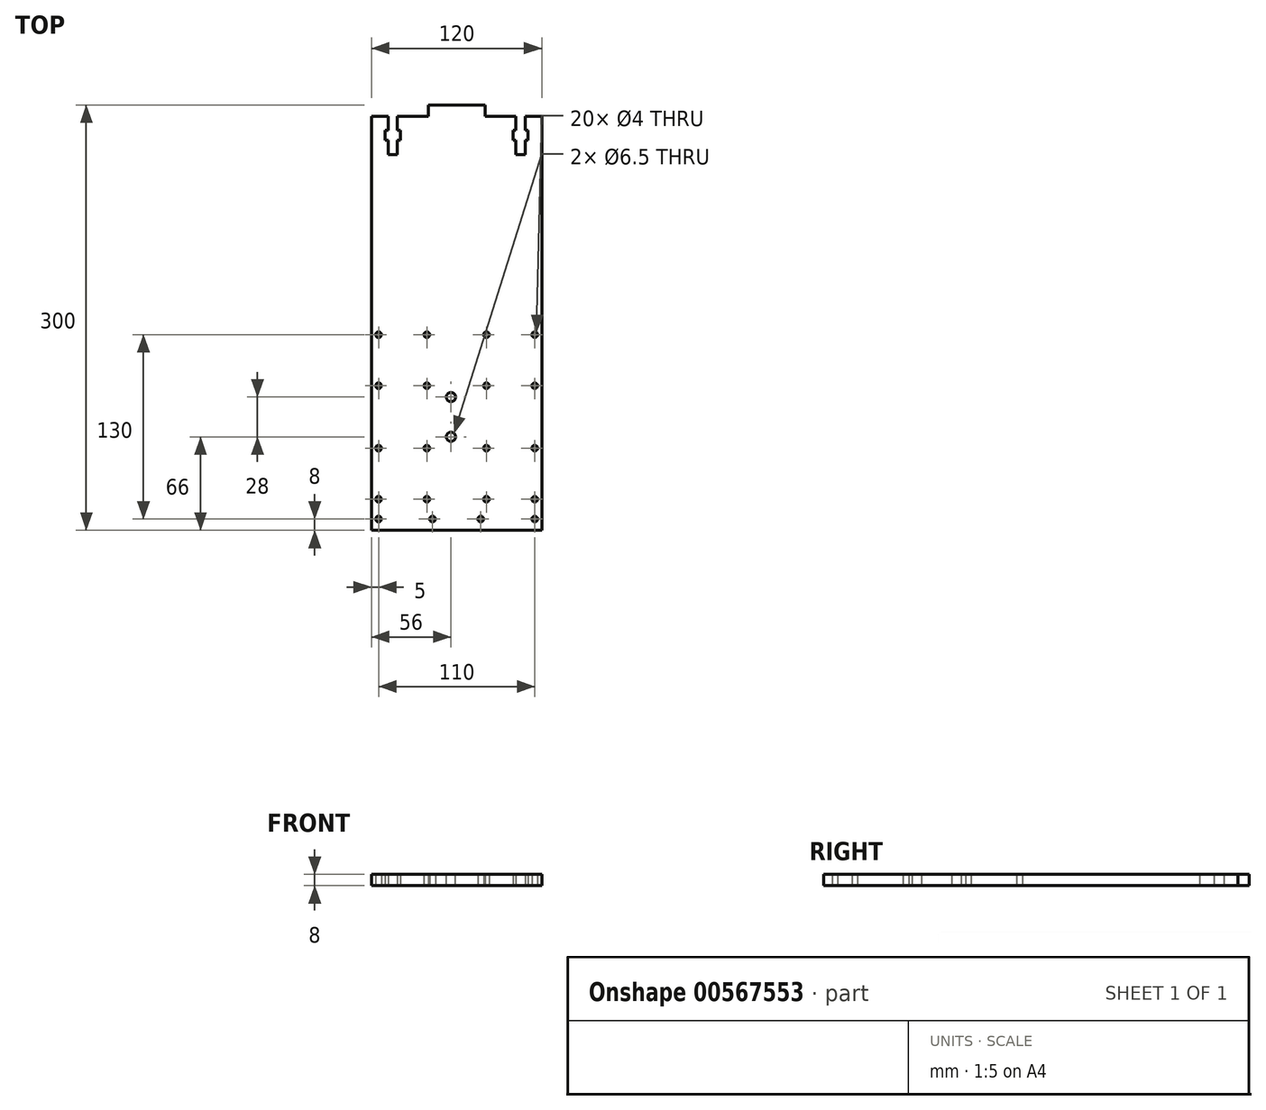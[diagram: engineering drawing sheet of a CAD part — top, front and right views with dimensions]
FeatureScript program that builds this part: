
annotation { "Feature Type Name" : "Feature", "Feature Type Description" : "" }
export const myFeature = defineFeature(function(context is Context, id is Id, definition is map)
    precondition{}
    {
        {
            var Q0;
            Q0=qCreatedBy(makeId("Top.planeOp"),FACE);
            var sketch = newSketch(context, id + "F0", { "sketchPlane" : qUnion([Q0])});
            skLineSegment(sketch, "E0.bottom", {"start": v(60, 212) * mm, "end": v(48.25, 212) * mm});
            skLineSegment(sketch, "E0.top", {"start": v(60, -80) * mm, "end": v(-60, -80) * mm});
            skLineSegment(sketch, "E0.left", {"start": v(60, 212) * mm, "end": v(60, -80) * mm});
            skLineSegment(sketch, "E0.right", {"start": v(-60, 212) * mm, "end": v(-60, -80) * mm});
            skPoint(sketch, "E0.middle", {"position": v(0, 66) * mm});
            skLineSegment(sketch, "E1.bottom", {"start": v(-55, 58) * mm, "end": v(-21, 58) * mm, "construction": true});
            skLineSegment(sketch, "E1.top", {"start": v(-55, 22) * mm, "end": v(-21, 22) * mm, "construction": true});
            skLineSegment(sketch, "E1.left", {"start": v(-55, 58) * mm, "end": v(-55, 22) * mm, "construction": true});
            skLineSegment(sketch, "E1.right", {"start": v(-21, 58) * mm, "end": v(-21, 22) * mm, "construction": true});
            skCircle(sketch, "E2", {"center": v(-55, 58) * mm, "radius": 2 * mm});
            skCircle(sketch, "E3", {"center": v(-21, 58) * mm, "radius": 2 * mm});
            skCircle(sketch, "E4", {"center": v(-21, 22) * mm, "radius": 2 * mm});
            skCircle(sketch, "E5", {"center": v(-55, 22) * mm, "radius": 2 * mm});
            skCircle(sketch, "E6.MirrorC", {"center": v(21, 58) * mm, "radius": 2 * mm});
            skCircle(sketch, "E7.MirrorC", {"center": v(55, 58) * mm, "radius": 2 * mm});
            skCircle(sketch, "E8.MirrorC", {"center": v(55, 22) * mm, "radius": 2 * mm});
            skCircle(sketch, "E9.MirrorC", {"center": v(21, 22) * mm, "radius": 2 * mm});
            skCircle(sketch, "E10.MirrorC", {"center": v(-55, -22) * mm, "radius": 2 * mm});
            skCircle(sketch, "E11.MirrorC", {"center": v(21, -22) * mm, "radius": 2 * mm});
            skCircle(sketch, "E12.MirrorC", {"center": v(55, -22) * mm, "radius": 2 * mm});
            skCircle(sketch, "E13.MirrorC", {"center": v(-21, -22) * mm, "radius": 2 * mm});
            skCircle(sketch, "E14.MirrorC", {"center": v(21, -58) * mm, "radius": 2 * mm});
            skCircle(sketch, "E15.MirrorC", {"center": v(55, -58) * mm, "radius": 2 * mm});
            skCircle(sketch, "E16.MirrorC", {"center": v(-21, -58) * mm, "radius": 2 * mm});
            skCircle(sketch, "E17.MirrorC", {"center": v(-55, -58) * mm, "radius": 2 * mm});
            skCircle(sketch, "E18", {"center": v(-55, -72) * mm, "radius": 2 * mm});
            skCircle(sketch, "E19", {"center": v(-17, -72) * mm, "radius": 2 * mm});
            skCircle(sketch, "E20", {"center": v(17, -72) * mm, "radius": 2 * mm});
            skCircle(sketch, "E21", {"center": v(55, -72) * mm, "radius": 2 * mm});
            skLineSegment(sketch, "E22", {"start": v(20, 220) * mm, "end": v(20, 212) * mm});
            skLineSegment(sketch, "E23", {"start": v(20, 220) * mm, "end": v(-20, 220) * mm});
            skLineSegment(sketch, "E24", {"start": v(-20, 212) * mm, "end": v(-20, 220) * mm});
            skLineSegment(sketch, "E25.trimOffspring", {"start": v(-20, 212) * mm, "end": v(-41.75, 212) * mm});
            skLineSegment(sketch, "E26", {"start": v(-41.75, 212) * mm, "end": v(-41.75, 202) * mm});
            skLineSegment(sketch, "E27", {"start": v(-41.75, 202) * mm, "end": v(-39.75, 202) * mm});
            skLineSegment(sketch, "E28", {"start": v(-39.75, 202) * mm, "end": v(-39.75, 195) * mm});
            skLineSegment(sketch, "E29", {"start": v(-39.75, 195) * mm, "end": v(-41.75, 195) * mm});
            skLineSegment(sketch, "E30", {"start": v(-41.75, 195) * mm, "end": v(-41.75, 185) * mm});
            skLineSegment(sketch, "E31", {"start": v(-41.75, 185) * mm, "end": v(-48.25, 185) * mm});
            skLineSegment(sketch, "E32", {"start": v(-48.25, 185) * mm, "end": v(-48.25, 195) * mm});
            skLineSegment(sketch, "E33", {"start": v(-48.25, 195) * mm, "end": v(-50.25, 195) * mm});
            skLineSegment(sketch, "E34", {"start": v(-50.25, 195) * mm, "end": v(-50.25, 202) * mm});
            skLineSegment(sketch, "E35", {"start": v(-50.25, 202) * mm, "end": v(-48.25, 202) * mm});
            skLineSegment(sketch, "E36", {"start": v(-48.25, 202) * mm, "end": v(-48.25, 212) * mm});
            skLineSegment(sketch, "E37.trimOffspring", {"start": v(-48.25, 212) * mm, "end": v(-60, 212) * mm});
            skLineSegment(sketch, "E38.MirrorCS", {"start": v(41.75, 185) * mm, "end": v(48.25, 185) * mm});
            skLineSegment(sketch, "E39.MirrorCS", {"start": v(41.75, 195) * mm, "end": v(41.75, 185) * mm});
            skLineSegment(sketch, "E40.MirrorCS", {"start": v(48.25, 185) * mm, "end": v(48.25, 195) * mm});
            skLineSegment(sketch, "E41.MirrorCS", {"start": v(48.25, 195) * mm, "end": v(50.25, 195) * mm});
            skLineSegment(sketch, "E42.MirrorCS", {"start": v(39.75, 195) * mm, "end": v(41.75, 195) * mm});
            skLineSegment(sketch, "E43.MirrorCS", {"start": v(39.75, 202) * mm, "end": v(39.75, 195) * mm});
            skLineSegment(sketch, "E44.MirrorCS", {"start": v(50.25, 195) * mm, "end": v(50.25, 202) * mm});
            skLineSegment(sketch, "E45.MirrorCS", {"start": v(50.25, 202) * mm, "end": v(48.25, 202) * mm});
            skLineSegment(sketch, "E46.MirrorCS", {"start": v(41.75, 202) * mm, "end": v(39.75, 202) * mm});
            skLineSegment(sketch, "E47.MirrorCS", {"start": v(41.75, 212) * mm, "end": v(41.75, 202) * mm});
            skLineSegment(sketch, "E48.MirrorCS", {"start": v(48.25, 202) * mm, "end": v(48.25, 212) * mm});
            skLineSegment(sketch, "E49.trimOffspring", {"start": v(41.75, 212) * mm, "end": v(20, 212) * mm});
            skSolve(sketch);
        }
        {
            var Q0;
            Q0 = qSketchRegion(id + "F0", true);
            extrude(context, id + "F1", {"entities" : qUnion([Q0]), "depth" : 8 * mm, "offsetDistance" : 25 * mm});
        }
        {
            var Q0;
            Q0=makeQuery(id+"F1.opExtrude","CAP_FACE",FACE,{"disambiguationData":[OSD([sQuery(id+"F0.wireOp",EDGE,"E0.bottom"),sQuery(id+"F0.wireOp",EDGE,"E0.top"),sQuery(id+"F0.wireOp",EDGE,"E0.left"),sQuery(id+"F0.wireOp",EDGE,"E0.right"),sQuery(id+"F0.wireOp",EDGE,"E2"),sQuery(id+"F0.wireOp",EDGE,"E3"),sQuery(id+"F0.wireOp",EDGE,"E4"),sQuery(id+"F0.wireOp",EDGE,"E5"),sQuery(id+"F0.wireOp",EDGE,"E6.MirrorC"),sQuery(id+"F0.wireOp",EDGE,"E7.MirrorC"),sQuery(id+"F0.wireOp",EDGE,"E8.MirrorC"),sQuery(id+"F0.wireOp",EDGE,"E9.MirrorC"),sQuery(id+"F0.wireOp",EDGE,"E10.MirrorC"),sQuery(id+"F0.wireOp",EDGE,"E11.MirrorC"),sQuery(id+"F0.wireOp",EDGE,"E12.MirrorC"),sQuery(id+"F0.wireOp",EDGE,"E13.MirrorC"),sQuery(id+"F0.wireOp",EDGE,"E14.MirrorC"),sQuery(id+"F0.wireOp",EDGE,"E15.MirrorC"),sQuery(id+"F0.wireOp",EDGE,"E16.MirrorC"),sQuery(id+"F0.wireOp",EDGE,"E17.MirrorC"),sQuery(id+"F0.wireOp",EDGE,"E18"),sQuery(id+"F0.wireOp",EDGE,"E19"),sQuery(id+"F0.wireOp",EDGE,"E20"),sQuery(id+"F0.wireOp",EDGE,"E21"),sQuery(id+"F0.wireOp",EDGE,"E22"),sQuery(id+"F0.wireOp",EDGE,"E23"),sQuery(id+"F0.wireOp",EDGE,"E24"),sQuery(id+"F0.wireOp",EDGE,"E25.trimOffspring"),sQuery(id+"F0.wireOp",EDGE,"E26"),sQuery(id+"F0.wireOp",EDGE,"E27"),sQuery(id+"F0.wireOp",EDGE,"E28"),sQuery(id+"F0.wireOp",EDGE,"E29"),sQuery(id+"F0.wireOp",EDGE,"E30"),sQuery(id+"F0.wireOp",EDGE,"E31"),sQuery(id+"F0.wireOp",EDGE,"E32"),sQuery(id+"F0.wireOp",EDGE,"E33"),sQuery(id+"F0.wireOp",EDGE,"E34"),sQuery(id+"F0.wireOp",EDGE,"E35"),sQuery(id+"F0.wireOp",EDGE,"E36"),sQuery(id+"F0.wireOp",EDGE,"E37.trimOffspring"),sQuery(id+"F0.wireOp",EDGE,"E38.MirrorCS"),sQuery(id+"F0.wireOp",EDGE,"E39.MirrorCS"),sQuery(id+"F0.wireOp",EDGE,"E40.MirrorCS"),sQuery(id+"F0.wireOp",EDGE,"E41.MirrorCS"),sQuery(id+"F0.wireOp",EDGE,"E42.MirrorCS"),sQuery(id+"F0.wireOp",EDGE,"E43.MirrorCS"),sQuery(id+"F0.wireOp",EDGE,"E44.MirrorCS"),sQuery(id+"F0.wireOp",EDGE,"E45.MirrorCS"),sQuery(id+"F0.wireOp",EDGE,"E46.MirrorCS"),sQuery(id+"F0.wireOp",EDGE,"E47.MirrorCS"),sQuery(id+"F0.wireOp",EDGE,"E48.MirrorCS"),sQuery(id+"F0.wireOp",EDGE,"E49.trimOffspring")])],"isStart":false});
            var sketch = newSketch(context, id + "F2", { "sketchPlane" : qUnion([Q0])});
            skCircle(sketch, "E50", {"center": v(-4, 14) * mm, "radius": 3.25 * mm});
            skCircle(sketch, "E51", {"center": v(-4, -14) * mm, "radius": 3.25 * mm});
            skSolve(sketch);
        }
        {
            var Q0;
            Q0 = qSketchRegion(id + "F2", true);
            extrude(context, id + "F3", {"entities" : qUnion([Q0]), "operationType" : NewBodyOperationType.REMOVE, "endBound" : BoundingType.THROUGH_ALL, "oppositeDirection" : true, "depth" : 25 * mm, "offsetDistance" : 25 * mm});
        }
    });
